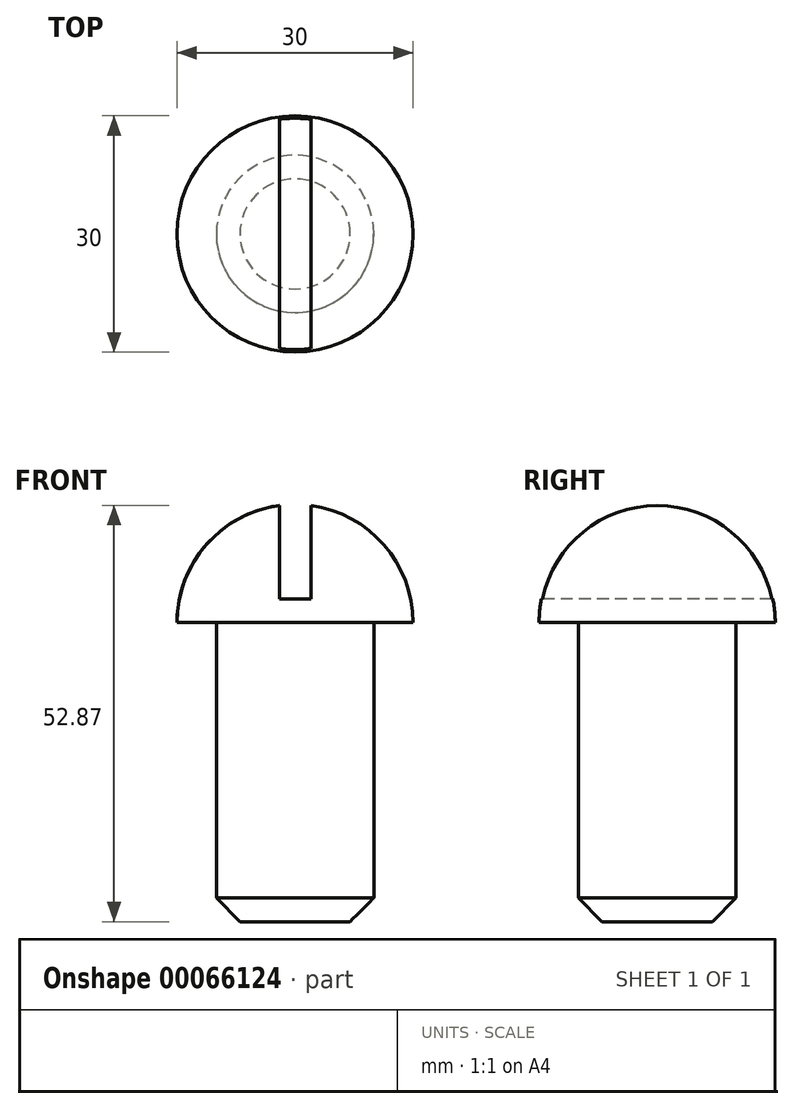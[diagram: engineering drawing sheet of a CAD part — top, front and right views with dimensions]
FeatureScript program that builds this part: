
annotation { "Feature Type Name" : "Feature", "Feature Type Description" : "" }
export const myFeature = defineFeature(function(context is Context, id is Id, definition is map)
    precondition{}
    {
        {
            var Q0;
            Q0=qCreatedBy(makeId("Front.planeOp"),FACE);
            var sketch = newSketch(context, id + "F0", { "sketchPlane" : qUnion([Q0])});
            skArc(sketch, "E0", {"start": v(0, 15) * mm, "mid": v(-10.6, 10.6) * mm, "end": v(-15, 0) * mm});
            skLineSegment(sketch, "E1", {"start": v(-15, 0) * mm, "end": v(-10, 0) * mm});
            skLineSegment(sketch, "E2", {"start": v(-10, 0) * mm, "end": v(-10, -38) * mm});
            skLineSegment(sketch, "E3", {"start": v(-10, -38) * mm, "end": v(0, -38) * mm});
            skLineSegment(sketch, "E4", {"start": v(0, -38) * mm, "end": v(0, 15) * mm});
            skSolve(sketch);
        }
        {
            var Q0;
            Q0=makeQuery(id+"F0.imprint","IMPRINT",FACE,{"disambiguationData":[TD([[makeQuery(id+"F0.imprint","IMPRINT",EDGE,{"derivedFrom":sQuery(id+"F0.wireOp",EDGE,"E0")}),1.0]])]});
            var Q1;
            Q1=sQuery(id+"F0.wireOp",EDGE,"E4");
            revolve(context, id + "F1", {"entities" : qUnion([Q0]), "axis" : qUnion([Q1]), "revolveType" : RevolveType.FULL});
        }
        {
            var Q0;
            Q0=makeQuery(id+"F1.opRevolve","SWEPT_FACE",FACE,{"disambiguationData":[OSD([sQuery(id+"F0.wireOp",EDGE,"E3")])]});
            chamfer(context, id + "F2", {"entities" : qUnion([Q0]), "width" : 3 * mm, "tangentPropagation" : true});
        }
        {
            var Q0;
            Q0=qCreatedBy(makeId("Front.planeOp"),FACE);
            var sketch = newSketch(context, id + "F3", { "sketchPlane" : qUnion([Q0])});
            skLineSegment(sketch, "E5.bottom", {"start": v(-2, 18.68) * mm, "end": v(2, 18.68) * mm});
            skLineSegment(sketch, "E5.top", {"start": v(-2, 3) * mm, "end": v(2, 3) * mm});
            skLineSegment(sketch, "E5.left", {"start": v(-2, 18.68) * mm, "end": v(-2, 3) * mm});
            skLineSegment(sketch, "E5.right", {"start": v(2, 18.68) * mm, "end": v(2, 3) * mm});
            skSolve(sketch);
        }
        {
            var Q0;
            Q0=makeQuery(id+"F3.imprint","IMPRINT",FACE,{"disambiguationData":[TD([[makeQuery(id+"F3.imprint","IMPRINT",EDGE,{"derivedFrom":sQuery(id+"F3.wireOp",EDGE,"E5.bottom")}),-1.0]])]});
            extrude(context, id + "F4", {"entities" : qUnion([Q0]), "operationType" : NewBodyOperationType.REMOVE, "endBound" : BoundingType.THROUGH_ALL, "oppositeDirection" : true, "depth" : 25 * mm, "hasSecondDirection" : true, "secondDirectionBound" : SecondDirectionBoundingType.THROUGH_ALL, "secondDirectionOppositeDirection" : false, "secondDirectionDepth" : 25 * mm});
        }
    });
